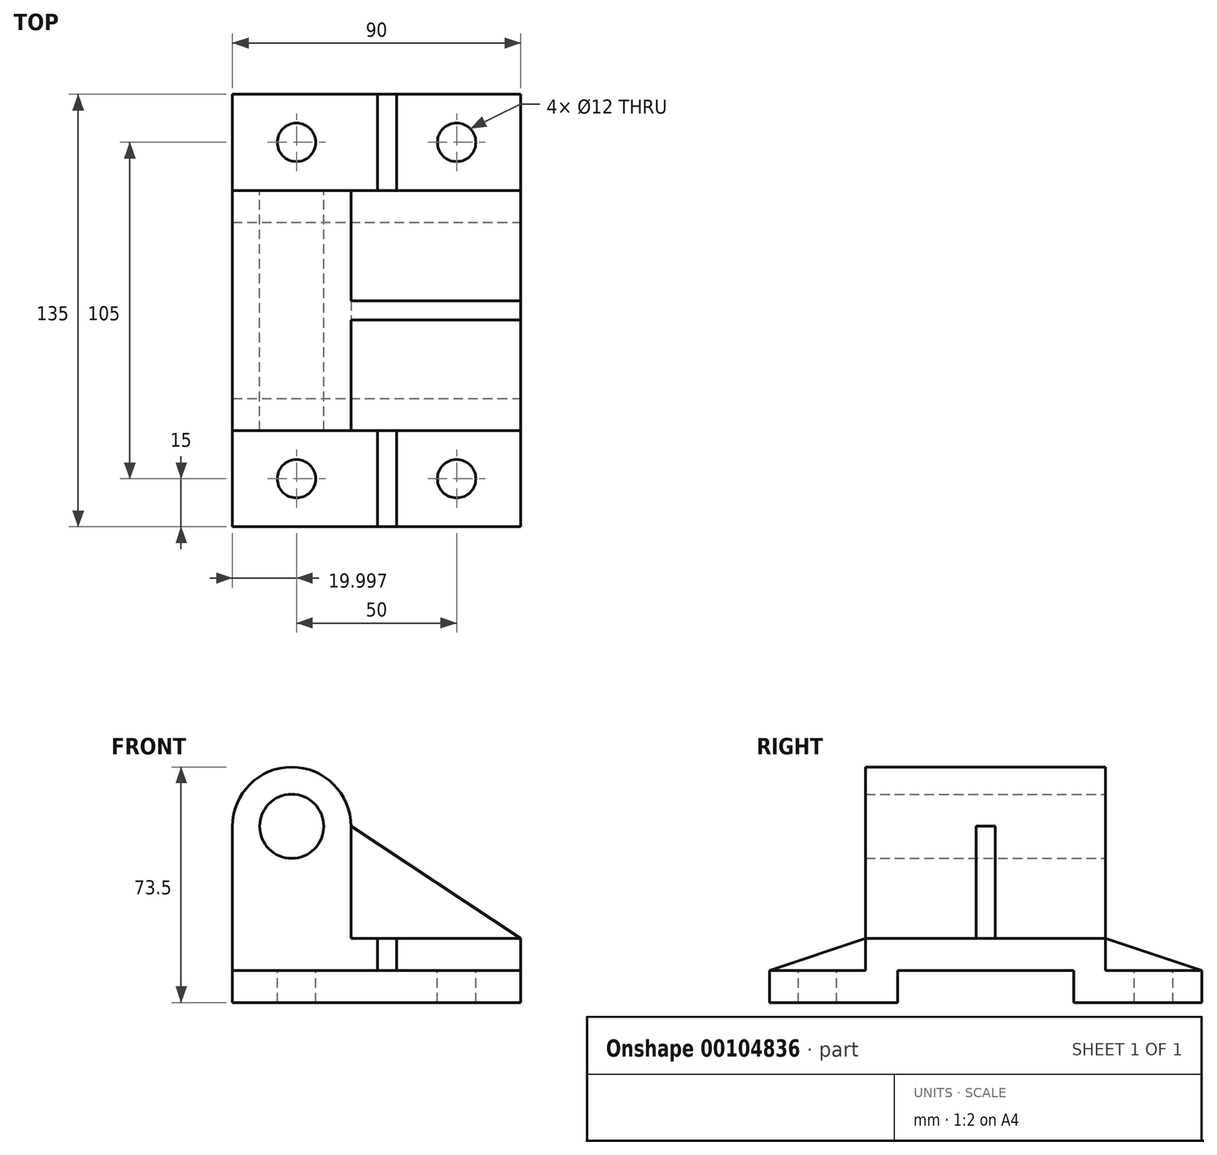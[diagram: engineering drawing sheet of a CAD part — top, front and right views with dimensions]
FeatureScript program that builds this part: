
annotation { "Feature Type Name" : "Feature", "Feature Type Description" : "" }
export const myFeature = defineFeature(function(context is Context, id is Id, definition is map)
    precondition{}
    {
        {
            var Q0;
            Q0=qCreatedBy(makeId("Front.planeOp"),FACE);
            var sketch = newSketch(context, id + "F0", { "sketchPlane" : qUnion([Q0])});
            skLineSegment(sketch, "E0", {"start": v(-38.27, 0) * mm, "end": v(51.73, 0) * mm});
            skLineSegment(sketch, "E1", {"start": v(51.73, 0) * mm, "end": v(51.73, 20) * mm});
            skLineSegment(sketch, "E2", {"start": v(51.73, 20) * mm, "end": v(-1.27, 20) * mm});
            skLineSegment(sketch, "E3", {"start": v(-1.27, 20) * mm, "end": v(-1.27, 55) * mm});
            skLineSegment(sketch, "E4", {"start": v(-38.27, 55) * mm, "end": v(-38.27, 0) * mm});
            skArc(sketch, "E5", {"start": v(-1.27, 55) * mm, "mid": v(-19.77, 73.5) * mm, "end": v(-38.27, 55) * mm});
            skCircle(sketch, "E6", {"center": v(-19.77, 55) * mm, "radius": 10 * mm});
            skSolve(sketch);
        }
        {
            var Q0;
            Q0=makeQuery(id+"F0.imprint","IMPRINT",FACE,{"disambiguationData":[TD([[makeQuery(id+"F0.imprint","IMPRINT",EDGE,{"derivedFrom":sQuery(id+"F0.wireOp",EDGE,"E0")}),1.0]])]});
            extrude(context, id + "F1", {"entities" : qUnion([Q0]), "depth" : 135 * mm, "symmetric" : true});
        }
        {
            var Q0;
            Q0=qCreatedBy(makeId("Right.planeOp"),FACE);
            var sketch = newSketch(context, id + "F2", { "sketchPlane" : qUnion([Q0])});
            skLineSegment(sketch, "E7.bottom", {"start": v(-27.5, 0) * mm, "end": v(27.5, 0) * mm});
            skLineSegment(sketch, "E7.top", {"start": v(-27.5, 10) * mm, "end": v(27.5, 10) * mm});
            skLineSegment(sketch, "E7.left", {"start": v(-27.5, 0) * mm, "end": v(-27.5, 10) * mm});
            skLineSegment(sketch, "E7.right", {"start": v(27.5, 0) * mm, "end": v(27.5, 10) * mm});
            skLineSegment(sketch, "E8.bottom", {"start": v(-67.5, 10) * mm, "end": v(-37.5, 10) * mm});
            skLineSegment(sketch, "E8.top", {"start": v(-67.5, 88.91) * mm, "end": v(-37.5, 88.91) * mm});
            skLineSegment(sketch, "E8.left", {"start": v(-67.5, 10) * mm, "end": v(-67.5, 88.91) * mm});
            skLineSegment(sketch, "E8.right", {"start": v(-37.5, 10) * mm, "end": v(-37.5, 88.91) * mm});
            skLineSegment(sketch, "E9.MirrorCS", {"start": v(67.5, 10) * mm, "end": v(67.5, 88.91) * mm});
            skLineSegment(sketch, "E10.MirrorCS", {"start": v(67.5, 10) * mm, "end": v(37.5, 10) * mm});
            skLineSegment(sketch, "E11.MirrorCS", {"start": v(37.5, 10) * mm, "end": v(37.5, 88.91) * mm});
            skLineSegment(sketch, "E12.MirrorCS", {"start": v(67.5, 88.91) * mm, "end": v(37.5, 88.91) * mm});
            skSolve(sketch);
        }
        {
            var Q0;
            Q0 = qSketchRegion(id + "F2", true);
            extrude(context, id + "F3", {"entities" : qUnion([Q0]), "operationType" : NewBodyOperationType.REMOVE, "oppositeDirection" : true, "depth" : 200 * mm, "symmetric" : true});
        }
        {
            var Q0;
            Q0=qCreatedBy(makeId("Top.planeOp"),FACE);
            var sketch = newSketch(context, id + "F4", { "sketchPlane" : qUnion([Q0])});
            skCircle(sketch, "E13", {"center": v(31.73, -52.5) * mm, "radius": 6 * mm});
            skCircle(sketch, "E14.0.1.0", {"center": v(31.73, 52.5) * mm, "radius": 6 * mm});
            skCircle(sketch, "E14.1.0.0", {"center": v(-18.27, -52.5) * mm, "radius": 6 * mm});
            skCircle(sketch, "E14.1.1.0", {"center": v(-18.27, 52.5) * mm, "radius": 6 * mm});
            skLineSegment(sketch, "E14.direction1", {"start": v(31.73, -52.5) * mm, "end": v(-18.27, -52.5) * mm, "construction": true});
            skLineSegment(sketch, "E14.direction2", {"start": v(31.73, -52.5) * mm, "end": v(31.73, 52.5) * mm, "construction": true});
            skSolve(sketch);
        }
        {
            var Q0;
            Q0 = qSketchRegion(id + "F4", true);
            extrude(context, id + "F5", {"entities" : qUnion([Q0]), "operationType" : NewBodyOperationType.REMOVE, "oppositeDirection" : true, "depth" : 25 * mm, "symmetric" : true});
        }
        {
            var Q0;
            Q0=qCreatedBy(makeId("Right.planeOp"),FACE);
            cPlane(context, id + "F6", {"entities" : qUnion([Q0]), "cplaneType" : CPlaneType.OFFSET, "offset" : 10 * mm, "width" : 150 * mm, "height" : 150 * mm});
        }
        {
            var Q0;
            Q0=qCreatedBy(id+"F6.planeOp",FACE);
            var sketch = newSketch(context, id + "F7", { "sketchPlane" : qUnion([Q0])});
            skLineSegment(sketch, "E15", {"start": v(-67.5, 10) * mm, "end": v(-37.5, 10) * mm});
            skLineSegment(sketch, "E16", {"start": v(-37.5, 10) * mm, "end": v(-37.5, 20) * mm});
            skLineSegment(sketch, "E17", {"start": v(-37.5, 20) * mm, "end": v(-67.5, 10) * mm});
            skLineSegment(sketch, "E18.MirrorCS", {"start": v(67.5, 10) * mm, "end": v(37.5, 10) * mm});
            skLineSegment(sketch, "E19.MirrorCS", {"start": v(37.5, 20) * mm, "end": v(67.5, 10) * mm});
            skLineSegment(sketch, "E20.MirrorCS", {"start": v(37.5, 10) * mm, "end": v(37.5, 20) * mm});
            skSolve(sketch);
        }
        {
            var Q0;
            Q0=makeQuery(id+"F7.imprint","IMPRINT",FACE,{"disambiguationData":[TD([[makeQuery(id+"F7.imprint","IMPRINT",EDGE,{"derivedFrom":sQuery(id+"F7.wireOp",EDGE,"E15")}),1.0]])]});
            var Q1;
            Q1=makeQuery(id+"F7.imprint","IMPRINT",FACE,{"disambiguationData":[TD([[makeQuery(id+"F7.imprint","IMPRINT",EDGE,{"derivedFrom":sQuery(id+"F7.wireOp",EDGE,"E18.MirrorCS")}),-1.0]])]});
            extrude(context, id + "F8", {"entities" : qUnion([Q0, Q1]), "operationType" : NewBodyOperationType.ADD, "depth" : 6 * mm, "symmetric" : true});
        }
        {
            var Q0;
            Q0=qCreatedBy(makeId("Front.planeOp"),FACE);
            var sketch = newSketch(context, id + "F9", { "sketchPlane" : qUnion([Q0])});
            skLineSegment(sketch, "E21", {"start": v(51.73, 20) * mm, "end": v(-1.28, 20) * mm});
            skLineSegment(sketch, "E22", {"start": v(-1.28, 20) * mm, "end": v(-1.28, 55.02) * mm});
            skLineSegment(sketch, "E23", {"start": v(-1.28, 55.02) * mm, "end": v(51.73, 20) * mm});
            skSolve(sketch);
        }
        {
            var Q0;
            Q0 = qSketchRegion(id + "F9", true);
            extrude(context, id + "F10", {"entities" : qUnion([Q0]), "operationType" : NewBodyOperationType.ADD, "depth" : 6 * mm, "symmetric" : true});
        }
    });
